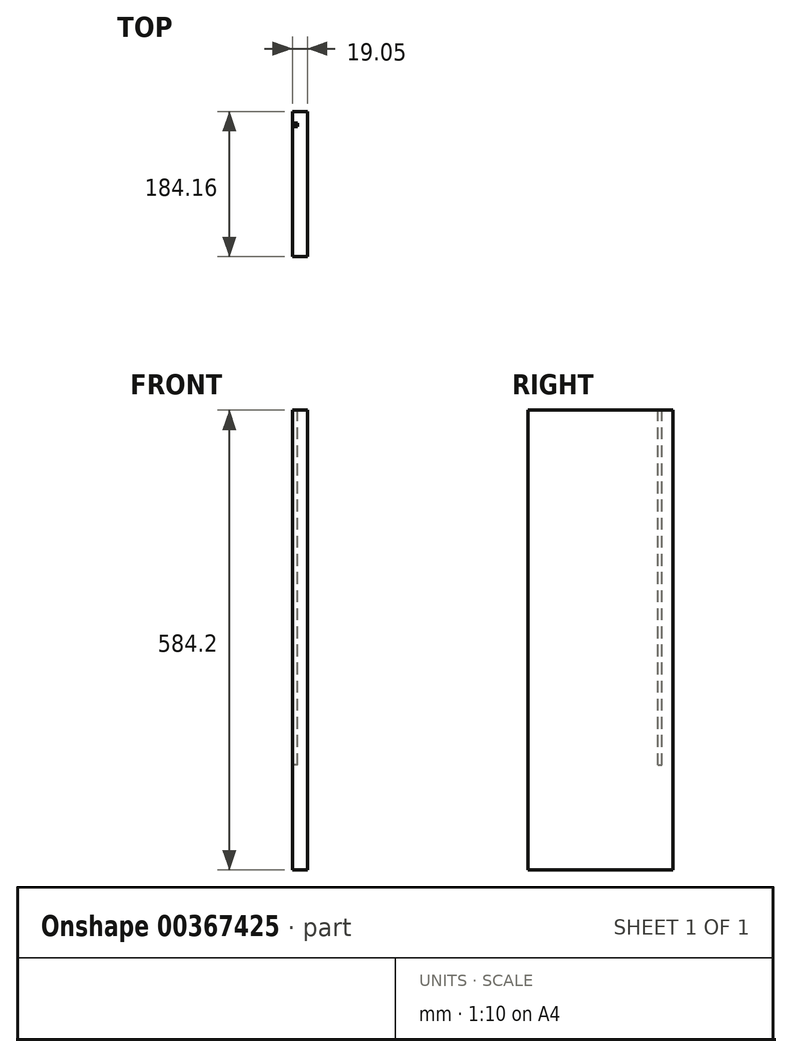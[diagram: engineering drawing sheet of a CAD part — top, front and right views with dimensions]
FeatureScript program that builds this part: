
annotation { "Feature Type Name" : "Feature", "Feature Type Description" : "" }
export const myFeature = defineFeature(function(context is Context, id is Id, definition is map)
    precondition{}
    {
        {
            var Q0;
            Q0=qCreatedBy(makeId("Right.planeOp"),FACE);
            var sketch = newSketch(context, id + "F0", { "sketchPlane" : qUnion([Q0])});
            skLineSegment(sketch, "E0.bottom", {"start": v(92.07, 292.1) * mm, "end": v(-92.08, 292.1) * mm});
            skLineSegment(sketch, "E0.top", {"start": v(92.08, -292.1) * mm, "end": v(-92.07, -292.1) * mm});
            skLineSegment(sketch, "E0.left", {"start": v(92.07, 292.1) * mm, "end": v(92.08, -292.1) * mm});
            skLineSegment(sketch, "E0.right", {"start": v(-92.08, 292.1) * mm, "end": v(-92.07, -292.1) * mm});
            skPoint(sketch, "E0.middle", {"position": v(0, 0) * mm});
            skSolve(sketch);
        }
        {
            var Q0;
            Q0 = qSketchRegion(id + "F0", true);
            extrude(context, id + "F1", {"entities" : qUnion([Q0]), "depth" : 19.05 * mm});
        }
        {
            var Q0;
            Q0=makeQuery(id+"F1.opExtrude","CAP_FACE",FACE,{"disambiguationData":[OSD([sQuery(id+"F0.wireOp",EDGE,"E0.bottom"),sQuery(id+"F0.wireOp",EDGE,"E0.top"),sQuery(id+"F0.wireOp",EDGE,"E0.left"),sQuery(id+"F0.wireOp",EDGE,"E0.right")])],"isStart":true});
            var sketch = newSketch(context, id + "F2", { "sketchPlane" : qUnion([Q0])});
            skLineSegment(sketch, "E1.bottom", {"start": v(-73.03, -158.75) * mm, "end": v(-77.79, -158.75) * mm});
            skLineSegment(sketch, "E1.top", {"start": v(-73.02, 292.1) * mm, "end": v(-77.79, 292.1) * mm});
            skLineSegment(sketch, "E1.left", {"start": v(-73.03, -158.75) * mm, "end": v(-73.02, 292.1) * mm});
            skLineSegment(sketch, "E1.right", {"start": v(-77.79, -158.75) * mm, "end": v(-77.79, 292.1) * mm});
            skSolve(sketch);
        }
        {
            var Q0;
            Q0 = qSketchRegion(id + "F2", true);
            extrude(context, id + "F3", {"entities" : qUnion([Q0]), "operationType" : NewBodyOperationType.REMOVE, "oppositeDirection" : true, "depth" : 6.35 * mm});
        }
    });
